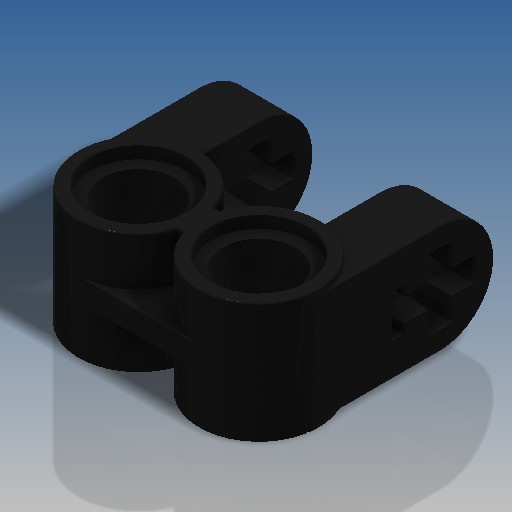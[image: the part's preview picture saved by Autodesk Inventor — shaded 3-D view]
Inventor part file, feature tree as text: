
AUTODESK INVENTOR PART (.ipt)
format: ipt  version: 2019.4 (Build 234330000, 330)  size: 354,816 bytes
history: native  units: mm
features: extrude x5, sketch x3, mirror x2, plane x1, fillet x1, projected_geometry x1
ambient origin geometry x8: Origin, YZ Plane, XZ Plane, XY Plane, X Axis, Y Axis, Z Axis, Center Point
bodies: Solid1 (feature_tree)
feature tree (13):
  sketch  "Sketch1"  dims[d0=8.0mm d2=8.0mm]
  extrude  "Extrusion1"  Depth=8.0mm
  extrude  "Extrusion13"  Depth=6.4mm
  plane  "Work Plane1"
  extrude  "Extrusion4"  Depth=0.1mm TaperAngle=0.0deg
  mirror  "Mirror2"
  extrude  "Extrusion14"  Depth=0.1mm
  mirror  "Mirror1"
  extrude  "Extrusion15"  Depth=0.1mm TaperAngle=0.0deg
  fillet  "Fillet1"  Radius=0.8mm
  sketch  "Sketch3"  dims[d3=4.8mm d4=6.4mm]
  projected_geometry  "Projected Loop1"
  sketch  "Sketch10"  dims[d7=8.0mm d8=0.0mm d15=4.0mm d16=0.0mm d35=2.4mm d36=1.6mm d37=0.0mm d38=0.8mm d39=0.0mm d47=4.8mm d49=7.2mm d50=0.8mm d51=2.8mm d52=8.0mm d53=1.6mm d54=0.9mm d55=0.0mm d56=0.1mm]
